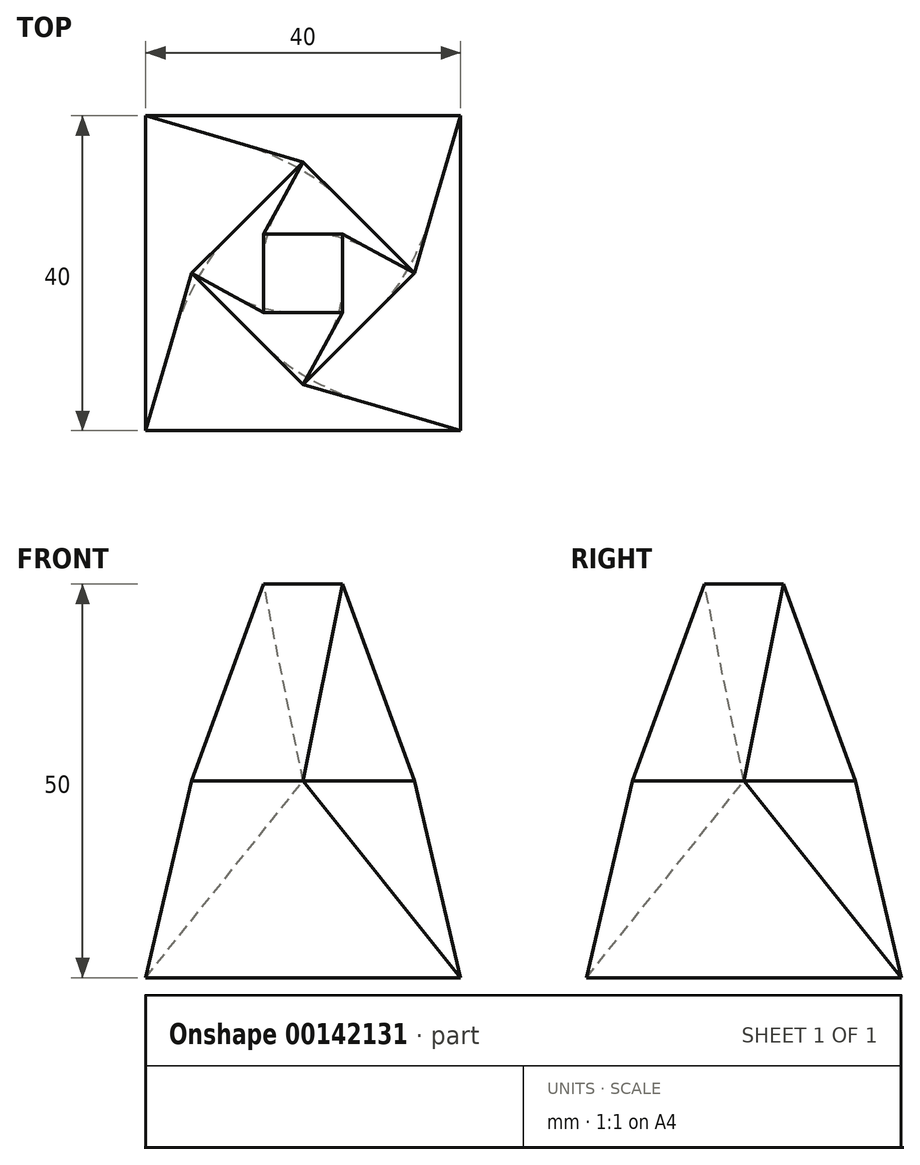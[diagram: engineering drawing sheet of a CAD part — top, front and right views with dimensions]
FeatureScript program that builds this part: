
annotation { "Feature Type Name" : "Feature", "Feature Type Description" : "" }
export const myFeature = defineFeature(function(context is Context, id is Id, definition is map)
    precondition{}
    {
        {
            var Q0;
            Q0=qCreatedBy(makeId("Top.planeOp"),FACE);
            var sketch = newSketch(context, id + "F0", { "sketchPlane" : qUnion([Q0])});
            skLineSegment(sketch, "E0.bottom", {"start": v(-20, 20) * mm, "end": v(20, 20) * mm});
            skLineSegment(sketch, "E0.top", {"start": v(-20, -20) * mm, "end": v(20, -20) * mm});
            skLineSegment(sketch, "E0.left", {"start": v(-20, 20) * mm, "end": v(-20, -20) * mm});
            skLineSegment(sketch, "E0.right", {"start": v(20, 20) * mm, "end": v(20, -20) * mm});
            skLineSegment(sketch, "E1", {"start": v(-20, -20) * mm, "end": v(20, 20) * mm, "construction": true});
            skSolve(sketch);
        }
        {
            var Q0;
            Q0=qCreatedBy(makeId("Top.planeOp"),FACE);
            cPlane(context, id + "F1", {"entities" : qUnion([Q0]), "cplaneType" : CPlaneType.OFFSET, "offset" : 25 * mm, "width" : 150 * mm, "height" : 150 * mm});
        }
        {
            var Q0;
            Q0=qCreatedBy(id+"F1.planeOp",FACE);
            var sketch = newSketch(context, id + "F2", { "sketchPlane" : qUnion([Q0])});
            skLineSegment(sketch, "E2", {"start": v(-14.14, 0) * mm, "end": v(0, -14.14) * mm});
            skLineSegment(sketch, "E3", {"start": v(0, -14.14) * mm, "end": v(14.14, 0) * mm});
            skLineSegment(sketch, "E4", {"start": v(14.14, 0) * mm, "end": v(0, 14.14) * mm});
            skLineSegment(sketch, "E5", {"start": v(0, 14.14) * mm, "end": v(-14.14, 0) * mm});
            skLineSegment(sketch, "E6", {"start": v(0, 14.14) * mm, "end": v(0, -14.14) * mm, "construction": true});
            skSolve(sketch);
        }
        {
            var Q0;
            Q0=makeQuery(id+"F0.imprint","IMPRINT",FACE,{"disambiguationData":[TD([[makeQuery(id+"F0.imprint","IMPRINT",EDGE,{"derivedFrom":sQuery(id+"F0.wireOp",EDGE,"E0.bottom")}),-1.0]])]});
            var Q1;
            Q1=makeQuery(id+"F2.imprint","IMPRINT",FACE,{"disambiguationData":[TD([[makeQuery(id+"F2.imprint","IMPRINT",EDGE,{"derivedFrom":sQuery(id+"F2.wireOp",EDGE,"E2")}),1.0]])]});
            loft(context, id + "F3", {"sheetProfilesArray" : [{ "sheetProfileEntities" : qUnion([Q0]) }, { "sheetProfileEntities" : qUnion([Q1]) }]});
        }
        {
            var Q0;
            Q0=qCreatedBy(id+"F1.planeOp",FACE);
            cPlane(context, id + "F4", {"entities" : qUnion([Q0]), "cplaneType" : CPlaneType.OFFSET, "offset" : 25 * mm, "width" : 150 * mm, "height" : 150 * mm});
        }
        {
            var Q0;
            Q0=qCreatedBy(id+"F4.planeOp",FACE);
            var sketch = newSketch(context, id + "F5", { "sketchPlane" : qUnion([Q0])});
            skLineSegment(sketch, "E7.bottom", {"start": v(5, 5) * mm, "end": v(-5, 5) * mm});
            skLineSegment(sketch, "E7.top", {"start": v(5, -5) * mm, "end": v(-5, -5) * mm});
            skLineSegment(sketch, "E7.left", {"start": v(5, 5) * mm, "end": v(5, -5) * mm});
            skLineSegment(sketch, "E7.right", {"start": v(-5, 5) * mm, "end": v(-5, -5) * mm});
            skLineSegment(sketch, "E8", {"start": v(-5, 5) * mm, "end": v(5, -5) * mm, "construction": true});
            skSolve(sketch);
        }
        {
            var Q1;
            Q1=makeQuery(id+"F3.opLoft","CAP_FACE",FACE,{"disambiguationData":[OSD([makeQuery(id+"F2.imprint","IMPRINT",FACE,{"disambiguationData":[TD([[makeQuery(id+"F2.imprint","IMPRINT",EDGE,{"derivedFrom":sQuery(id+"F2.wireOp",EDGE,"E2")}),1.0]])]})])],"isStart":true});
            var Q2;
            Q2=makeQuery(id+"F5.imprint","IMPRINT",FACE,{"disambiguationData":[TD([[makeQuery(id+"F5.imprint","IMPRINT",EDGE,{"derivedFrom":sQuery(id+"F5.wireOp",EDGE,"E7.bottom")}),1.0]])]});
            loft(context, id + "F6", {"operationType" : NewBodyOperationType.ADD, "sheetProfilesArray" : [{ "sheetProfileEntities" : qUnion([Q1]) }, { "sheetProfileEntities" : qUnion([Q2]) }]});
        }
    });
